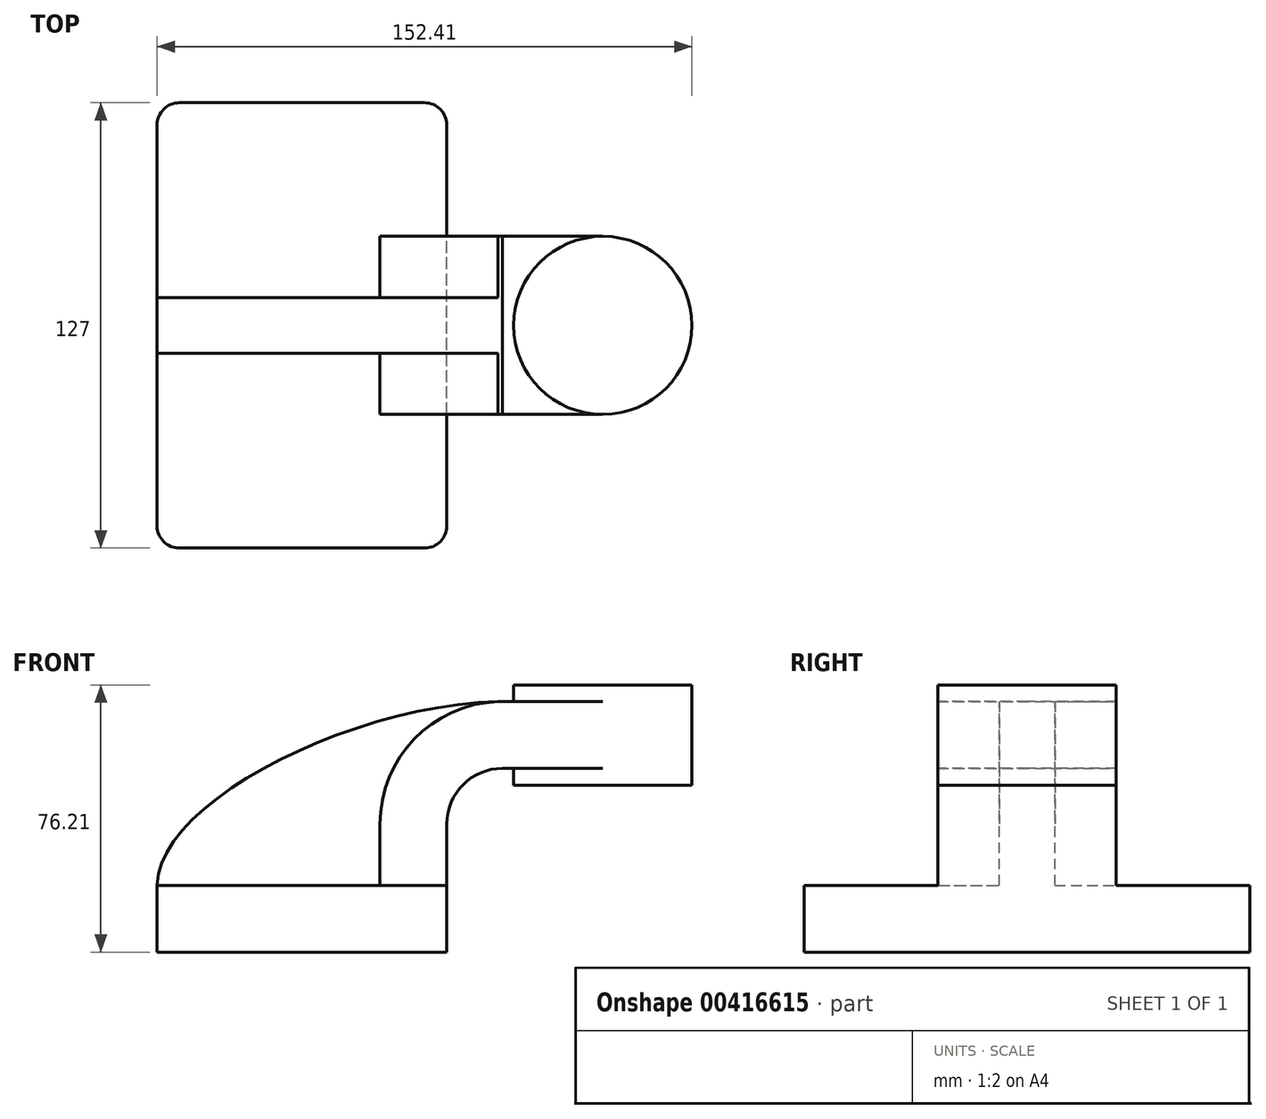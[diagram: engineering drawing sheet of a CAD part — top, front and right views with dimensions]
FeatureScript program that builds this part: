
annotation { "Feature Type Name" : "Feature", "Feature Type Description" : "" }
export const myFeature = defineFeature(function(context is Context, id is Id, definition is map)
    precondition{}
    {
        {
            var Q0;
            Q0=qCreatedBy(makeId("Front.planeOp"),FACE);
            var sketch = newSketch(context, id + "F0", { "sketchPlane" : qUnion([Q0])});
            skLineSegment(sketch, "E0.bottom", {"start": v(-41.28, -9.53) * mm, "end": v(41.28, -9.53) * mm});
            skLineSegment(sketch, "E0.top", {"start": v(-41.28, 9.53) * mm, "end": v(41.28, 9.53) * mm});
            skLineSegment(sketch, "E0.left", {"start": v(-41.28, -9.53) * mm, "end": v(-41.28, 9.53) * mm});
            skLineSegment(sketch, "E0.right", {"start": v(41.28, -9.53) * mm, "end": v(41.28, 9.52) * mm});
            skPoint(sketch, "E0.middle", {"position": v(0, 0) * mm});
            skLineSegment(sketch, "E1.bottom", {"start": v(60.32, 38.1) * mm, "end": v(111.12, 38.1) * mm});
            skLineSegment(sketch, "E1.top", {"start": v(60.32, 66.67) * mm, "end": v(111.12, 66.67) * mm});
            skLineSegment(sketch, "E1.left", {"start": v(60.32, 38.1) * mm, "end": v(60.32, 66.67) * mm});
            skLineSegment(sketch, "E1.right", {"start": v(111.12, 38.1) * mm, "end": v(111.12, 66.67) * mm});
            skPoint(sketch, "E1.middle", {"position": v(85.72, 52.39) * mm});
            skLineSegment(sketch, "E2", {"start": v(41.28, 9.52) * mm, "end": v(41.28, 27) * mm});
            skArc(sketch, "E3", {"start": v(41.27, 27) * mm, "mid": v(45.92, 38.23) * mm, "end": v(57.15, 42.88) * mm});
            skLineSegment(sketch, "E4", {"start": v(57.15, 42.88) * mm, "end": v(85.72, 42.88) * mm});
            skLineSegment(sketch, "E5.0", {"start": v(57.15, 61.93) * mm, "end": v(85.72, 61.93) * mm});
            skArc(sketch, "E5.1", {"start": v(22.22, 27) * mm, "mid": v(32.45, 51.7) * mm, "end": v(57.15, 61.93) * mm});
            skLineSegment(sketch, "E5.2", {"start": v(22.23, 9.52) * mm, "end": v(22.23, 27) * mm});
            skFitSpline(sketch, "E6", {"points": [v(-41.28, 9.53) * mm, v(57.15, 61.93) * mm], "startDerivative": vector(0.63, 71.17) * mm, "endDerivative": vector(128.36, 1.57) * mm});
            skLineSegment(sketch, "E7", {"start": v(85.72, 38.1) * mm, "end": v(85.72, 66.67) * mm});
            skSolve(sketch);
        }
        {
            var Q0;
            Q0=makeQuery(id+"F0.imprint","IMPRINT",FACE,{"disambiguationData":[TD([[makeQuery(id+"F0.imprint","IMPRINT",EDGE,{"derivedFrom":sQuery(id+"F0.wireOp",EDGE,"E0.bottom")}),1.0]])]});
            extrude(context, id + "F1", {"entities" : qUnion([Q0]), "endBound" : BoundingType.SYMMETRIC, "depth" : 127 * mm});
        }
        {
            var Q0;
            {var subQ1=sQuery(id+"F0.wireOp",EDGE,"E2");Q0=makeQuery(id+"F0.imprint","IMPRINT",FACE,{"disambiguationData":[TD([[makeQuery(id+"F0.imprint","IMPRINT",EDGE,{"derivedFrom":subQ1}),1.0]])]});}
            var Q1;
            {var subQ0=sQuery(id+"F0.wireOp",EDGE,"E4");var subQ1=sQuery(id+"F0.wireOp",EDGE,"E1.left");var subQ2=makeQuery(id+"F0.imprint","INTERSECT",VERTEX,{"derivedFrom":[subQ1,subQ0]});Q1=makeQuery(id+"F0.imprint","IMPRINT",FACE,{"disambiguationData":[TD([[makeQuery(id+"F0.imprint","IMPRINT",EDGE,{"disambiguationData":[TD([[subQ2,-1.0]])],"derivedFrom":subQ1}),-1.0]])]});}
            extrude(context, id + "F2", {"entities" : qUnion([Q0, Q1]), "operationType" : NewBodyOperationType.ADD, "endBound" : BoundingType.SYMMETRIC, "depth" : 50.8 * mm});
        }
        {
            var Q0;
            {var subQ3=sQuery(id+"F0.wireOp",EDGE,"E5.2");Q0=makeQuery(id+"F0.imprint","IMPRINT",FACE,{"disambiguationData":[TD([[makeQuery(id+"F0.imprint","IMPRINT",EDGE,{"derivedFrom":subQ3}),1.0]])]});}
            extrude(context, id + "F3", {"entities" : qUnion([Q0]), "operationType" : NewBodyOperationType.ADD, "endBound" : BoundingType.SYMMETRIC, "depth" : 15.88 * mm});
        }
        {
            var Q0;
            {var subQ4=sQuery(id+"F0.wireOp",EDGE,"E1.right");Q0=makeQuery(id+"F0.imprint","IMPRINT",FACE,{"disambiguationData":[TD([[makeQuery(id+"F0.imprint","IMPRINT",EDGE,{"derivedFrom":subQ4}),1.0]])]});}
            var Q1;
            Q1=sQuery(id+"F0.wireOp",EDGE,"E7");
            revolve(context, id + "F4", {"operationType" : NewBodyOperationType.ADD, "entities" : qUnion([Q0]), "axis" : qUnion([Q1]), "revolveType" : RevolveType.FULL});
        }
        {
            var Q0;
            Q0=makeQuery(id+"F1.opExtrude","CAP_EDGE",EDGE,{"disambiguationData":[OSD([sQuery(id+"F0.wireOp",EDGE,"E0.right")])],"isStart":true});
            var Q1;
            Q1=makeQuery(id+"F1.opExtrude","CAP_EDGE",EDGE,{"disambiguationData":[OSD([sQuery(id+"F0.wireOp",EDGE,"E0.left")])],"isStart":true});
            var Q2;
            Q2=makeQuery(id+"F1.opExtrude","CAP_EDGE",EDGE,{"disambiguationData":[OSD([sQuery(id+"F0.wireOp",EDGE,"E0.left")])],"isStart":false});
            var Q3;
            Q3=makeQuery(id+"F1.opExtrude","CAP_EDGE",EDGE,{"disambiguationData":[OSD([sQuery(id+"F0.wireOp",EDGE,"E0.right")])],"isStart":false});
            fillet(context, id + "F5", {"entities" : qUnion([Q0, Q1, Q2, Q3]), "radius" : 6.35 * mm, "tangentPropagation" : true, "allowEdgeOverflow" : false});
        }
    });
